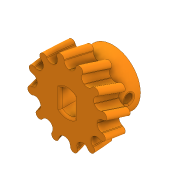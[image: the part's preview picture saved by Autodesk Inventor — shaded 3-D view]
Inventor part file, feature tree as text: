
AUTODESK INVENTOR PART (.ipt)
format: ipt  version: 2020 (Build 240168000, 168)  size: 770,560 bytes
history: native  units: in
note: dims shown in document units (in); Inventor stores cm internally (conversion verified against a paired STEP export)
features: sketch x10, extrude x6, projected_geometry x3, sweep x2, fillet x2, plane x1, other x1
ambient origin geometry x8: Origin, YZ Plane, XZ Plane, XY Plane, X Axis, Y Axis, Z Axis, Center Point
bodies: Solid1 (feature_tree)
feature tree (25):
  extrude  "Extrusion1"  Depth=0.315in
  plane  "Work Plane1"
  sweep  "Sweep1"
  extrude  "Extrusion3"  Depth=0.0866in
  extrude  "Extrusion4"  Depth=0.0787in
  extrude  "Extrusion5"  Depth=4.7244in TaperAngle=360.0deg
  extrude  "Extrusion6"  TaperAngle=0.0deg  [1 undecoded]
  fillet  "Fillet1"  Radius=1.0in
  sweep  "Sweep2"
  extrude  "Extrusion7"  Depth=0.0197in TaperAngle=0.0deg
  fillet  "Fillet3"  Radius=0.0748in
  sketch  "Sketch1"  dims[d0=0.4724in d1=0.315in]
  sketch  "Sketch3"  dims[d2=2.5197in d3=0.0in d7=-0.1969in]
  sketch  "3D Sketch1"
  other  "Helical Curve1"
  sketch  "Sketch4"  dims[d8=0.7087in d9=0.0866in]
  projected_geometry  "Projected Loop1"
  sketch  "Sketch5"  dims[d10=0.0787in d11=0.0787in]
  sketch  "Sketch6"  dims[d12=0.0787in d13=4.7244in d15=360.0deg]
  sketch  "Sketch7"  dims[d17=0.1969in d18=0.0118in d19=0.535in d20=0.0in d21=0.0in d22=0.0in d23=1.0in d24=0.0in]
  sketch  "Sketch8"  dims[d25=0.2008in d26=1.0in d27=0.0in]
  projected_geometry  "Projected Loop2"
  sketch  "3D Sketch2"
  sketch  "Sketch9"  dims[d28=0.1378in d29=0.1969in d30=0.0in d31=0.0748in d32=0.1969in d33=0.0in d34=0.0118in d39=0.0079in d40=0.0in d41=0.0in d42=0.122in d43=0.061in d44=1.0in d45=0.0in d46=0.0197in]
  projected_geometry  "Projected Loop3"
note: 1 required parameter value undecoded (feature->parameter linkage not recoverable at this tier; creation-order binding heuristic only, values carry confidence <= 0.55)
